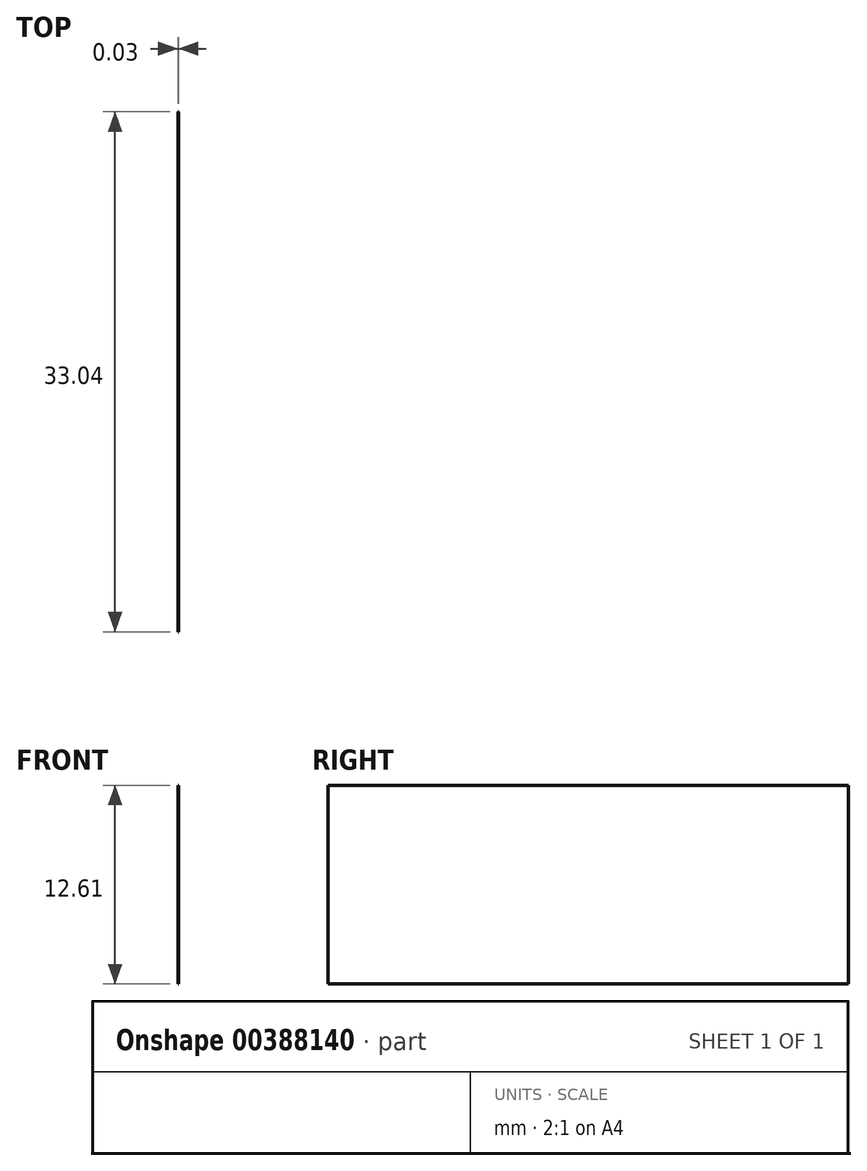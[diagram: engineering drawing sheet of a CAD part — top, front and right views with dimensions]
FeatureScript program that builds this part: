
annotation { "Feature Type Name" : "Feature", "Feature Type Description" : "" }
export const myFeature = defineFeature(function(context is Context, id is Id, definition is map)
    precondition{}
    {
        {
            var Q0;
            Q0=qCreatedBy(makeId("Right.planeOp"),FACE);
            var sketch = newSketch(context, id + "F0", { "sketchPlane" : qUnion([Q0])});
            skLineSegment(sketch, "E0", {"start": v(-55.38, 33.8) * mm, "end": v(-42.58, 33.8) * mm});
            skLineSegment(sketch, "E1", {"start": v(-42.58, 33.8) * mm, "end": v(-42.58, 23.3) * mm});
            skLineSegment(sketch, "E2", {"start": v(-42.58, 23.3) * mm, "end": v(-55, 23.3) * mm});
            skLineSegment(sketch, "E3", {"start": v(-55, 23.3) * mm, "end": v(-55.38, 33.8) * mm});
            skSolve(sketch);
        }
        {
            var Q0;
            Q0=makeQuery(id+"F0.imprint","IMPRINT",FACE,{"disambiguationData":[TD([[makeQuery(id+"F0.imprint","IMPRINT",EDGE,{"derivedFrom":sQuery(id+"F0.wireOp",EDGE,"E0")}),-1.0]])]});
            extrude(context, id + "F1", {"entities" : qUnion([Q0]), "depth" : 0.03 * mm});
        }
        {
            var Q0;
            Q0=qCreatedBy(makeId("Right.planeOp"),FACE);
            var sketch = newSketch(context, id + "F2", { "sketchPlane" : qUnion([Q0])});
            skLineSegment(sketch, "E4", {"start": v(-30.17, 37.43) * mm, "end": v(-30.17, 23.68) * mm});
            skLineSegment(sketch, "E5", {"start": v(-30.17, 23.68) * mm, "end": v(-15.47, 23.68) * mm});
            skLineSegment(sketch, "E6", {"start": v(-30.17, 37.43) * mm, "end": v(-15.85, 37.43) * mm});
            skLineSegment(sketch, "E7", {"start": v(-15.85, 37.43) * mm, "end": v(-15.47, 23.68) * mm});
            skSolve(sketch);
        }
        {
            var Q0;
            Q0=makeQuery(id+"F1.opExtrude","SWEPT_BODY",BODY,{"disambiguationData":[OSD([sQuery(id+"F0.wireOp",EDGE,"E0"),sQuery(id+"F0.wireOp",EDGE,"E1"),sQuery(id+"F0.wireOp",EDGE,"E2"),sQuery(id+"F0.wireOp",EDGE,"E3")])]});
            deleteBodies(context, id + "F3", {"entities" : qUnion([Q0])});
        }
        {
            var Q0;
            Q0=makeQuery(id+"F2.imprint","IMPRINT",FACE,{"disambiguationData":[TD([[makeQuery(id+"F2.imprint","IMPRINT",EDGE,{"derivedFrom":sQuery(id+"F2.wireOp",EDGE,"E4")}),1.0]])]});
            extrude(context, id + "F4", {"entities" : qUnion([Q0]), "depth" : 0.03 * mm});
        }
        {
            var Q0;
            Q0=qCreatedBy(makeId("Right.planeOp"),FACE);
            var sketch = newSketch(context, id + "F5", { "sketchPlane" : qUnion([Q0])});
            skLineSegment(sketch, "E8", {"start": v(9.74, 37.43) * mm, "end": v(42.78, 37.43) * mm});
            skLineSegment(sketch, "E9", {"start": v(42.78, 37.43) * mm, "end": v(42.78, 24.82) * mm});
            skLineSegment(sketch, "E10", {"start": v(42.78, 24.82) * mm, "end": v(9.74, 24.82) * mm});
            skLineSegment(sketch, "E11", {"start": v(9.74, 24.82) * mm, "end": v(9.74, 37.43) * mm});
            skSolve(sketch);
        }
        {
            var Q0;
            Q0=makeQuery(id+"F4.opExtrude","SWEPT_BODY",BODY,{"disambiguationData":[OSD([sQuery(id+"F2.wireOp",EDGE,"E4"),sQuery(id+"F2.wireOp",EDGE,"E5"),sQuery(id+"F2.wireOp",EDGE,"E6"),sQuery(id+"F2.wireOp",EDGE,"E7")])]});
            deleteBodies(context, id + "F6", {"entities" : qUnion([Q0])});
        }
        {
            var Q0;
            Q0=makeQuery(id+"F5.imprint","IMPRINT",FACE,{"disambiguationData":[TD([[makeQuery(id+"F5.imprint","IMPRINT",EDGE,{"derivedFrom":sQuery(id+"F5.wireOp",EDGE,"E8")}),-1.0]])]});
            extrude(context, id + "F7", {"entities" : qUnion([Q0]), "depth" : 0.03 * mm});
        }
    });
